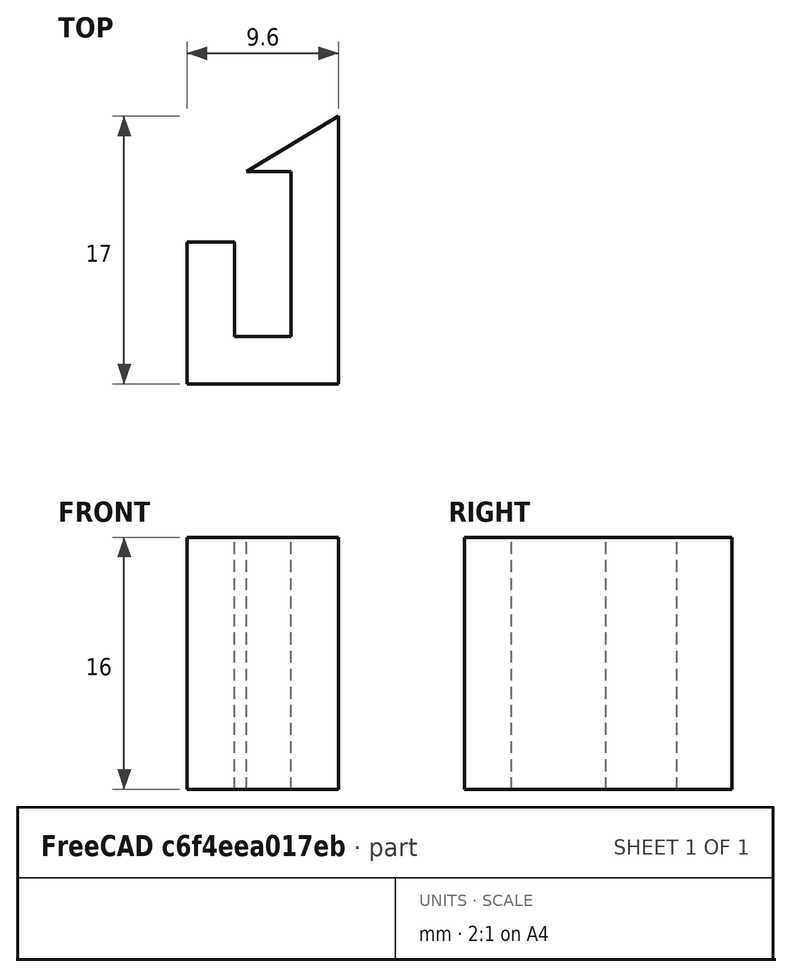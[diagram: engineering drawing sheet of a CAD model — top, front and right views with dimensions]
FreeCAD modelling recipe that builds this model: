
FCSTD DOCUMENT  (FreeCAD 0.14R3702 (Git))
Label: pinza_bugaboo
License: CC-BY 3.0
LicenseURL: http://creativecommons.org/licenses/by/3.0/
objects: Sketcher::SketchObject×1, PartDesign::Pad×1
note: 3 computed .brp shape members not serialized (recipe doc carries the construction recipe); baked Part::Feature solids carry a one-line shape summary decoded from their .brp

FEATURE [Sketcher::SketchObject] Sketch
  sketch-geometry (9):
    g0: LineSegment StartX=-4.8 StartY=1.56938 StartZ=0 EndX=-1.8 EndY=1.56938 EndZ=0
    g1: LineSegment StartX=-1.8 StartY=1.56938 StartZ=0 EndX=-1.8 EndY=-4.43062 EndZ=0
    g2: LineSegment StartX=-1.8 StartY=-4.43062 StartZ=0 EndX=1.8 EndY=-4.43062 EndZ=0
    g3: LineSegment StartX=1.8 StartY=-4.43062 StartZ=0 EndX=1.8 EndY=6.06938 EndZ=0
    g4: LineSegment StartX=1.8 StartY=6.06938 StartZ=0 EndX=-1.02418 EndY=6.06938 EndZ=0
    g5: LineSegment StartX=-1.02418 StartY=6.06938 StartZ=0 EndX=4.8 EndY=9.56938 EndZ=0
    g6: LineSegment StartX=4.8 StartY=9.56938 StartZ=0 EndX=4.8 EndY=-7.43062 EndZ=0
    g7: LineSegment StartX=4.8 StartY=-7.43062 StartZ=0 EndX=-4.8 EndY=-7.43062 EndZ=0
    g8: LineSegment StartX=-4.8 StartY=-7.43062 StartZ=0 EndX=-4.8 EndY=1.56938 EndZ=0
  constraints (24):
    c: Horizontal(g0)
    c: Coincident(g0,g1)
    c: Vertical(g1)
    c: Coincident(g1,g2)
    c: Horizontal(g2)
    c: Coincident(g2,g3)
    c: Vertical(g3)
    c: Coincident(g3,g4)
    c: Horizontal(g4)
    c: Coincident(g4,g5)
    c: Coincident(g5,g6)
    c: Vertical(g6)
    c: Coincident(g6,g7)
    c: Coincident(g7,g8)
    c: Coincident(g8,g0)
    c: Vertical(g8)
    c: DistanceY(g3) = 10.5
    c: DistanceX(g2) = 3.6
    c: DistanceX(g0) = 3
    c: Symmetric(g7,g6,g-2)
    c: DistanceX(g7) = -9.6
    c: DistanceY(g6) = -17
    c: Distance(g1,g7) = 3
    c: DistanceY(g8) = 9
FEATURE [PartDesign::Pad] Pad
  Length = 16
  Length2 = 100
  Sketch = -> Sketch
  Type = 0
